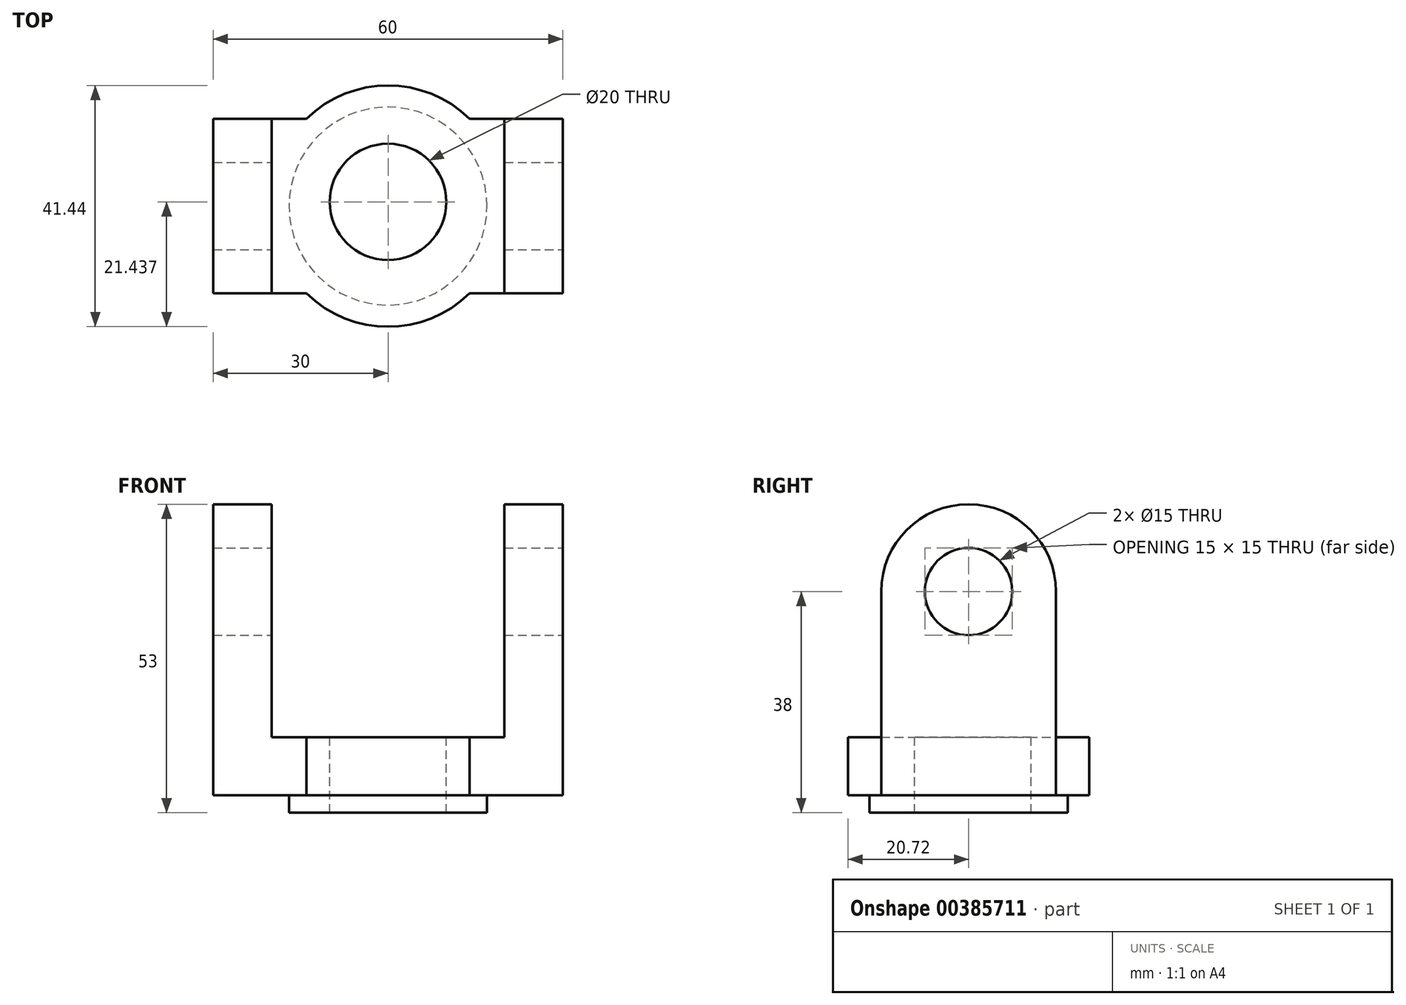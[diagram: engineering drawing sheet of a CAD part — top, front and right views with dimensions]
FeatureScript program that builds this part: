
annotation { "Feature Type Name" : "Feature", "Feature Type Description" : "" }
export const myFeature = defineFeature(function(context is Context, id is Id, definition is map)
    precondition{}
    {
        {
            var Q0;
            Q0=qCreatedBy(makeId("Front.planeOp"),FACE);
            var sketch = newSketch(context, id + "F0", { "sketchPlane" : qUnion([Q0])});
            skLineSegment(sketch, "E0", {"start": v(0, 0) * mm, "end": v(0, 35) * mm});
            skLineSegment(sketch, "E1", {"start": v(0, 35) * mm, "end": v(10, 35) * mm});
            skLineSegment(sketch, "E2", {"start": v(10, 35) * mm, "end": v(10, 10) * mm});
            skLineSegment(sketch, "E3", {"start": v(10, 10) * mm, "end": v(50, 10) * mm});
            skLineSegment(sketch, "E4", {"start": v(50, 10) * mm, "end": v(50, 35) * mm});
            skLineSegment(sketch, "E5", {"start": v(50, 35) * mm, "end": v(60, 35) * mm});
            skLineSegment(sketch, "E6", {"start": v(60, 35) * mm, "end": v(60, 0) * mm});
            skLineSegment(sketch, "E7", {"start": v(0, 0) * mm, "end": v(60, 0) * mm});
            skSolve(sketch);
        }
        {
            var Q0;
            Q0 = qSketchRegion(id + "F0", true);
            extrude(context, id + "F1", {"entities" : qUnion([Q0]), "depth" : 30 * mm});
        }
        {
            var Q0;
            Q0=qCreatedBy(makeId("Right.planeOp"),FACE);
            var sketch = newSketch(context, id + "F2", { "sketchPlane" : qUnion([Q0])});
            skArc(sketch, "E8", {"start": v(0, 35) * mm, "mid": v(-15, 50) * mm, "end": v(-30, 35) * mm});
            skLineSegment(sketch, "E9", {"start": v(-30, 35) * mm, "end": v(0, 35) * mm});
            skSolve(sketch);
        }
        {
            var Q0;
            Q0 = qSketchRegion(id + "F2", true);
            extrude(context, id + "F3", {"entities" : qUnion([Q0]), "operationType" : NewBodyOperationType.ADD, "depth" : 60 * mm});
        }
        {
            var Q0;
            Q0=makeQuery(id+"F3.boolean.opBoolean","MERGE",FACE,{"derivedFrom":[makeQuery(id+"F1.opExtrude","SWEPT_FACE",FACE,{"disambiguationData":[OSD([sQuery(id+"F0.wireOp",EDGE,"E6")])]}),makeQuery(id+"F3.opExtrude","CAP_FACE",FACE,{"disambiguationData":[OSD([sQuery(id+"F2.wireOp",EDGE,"E8"),sQuery(id+"F2.wireOp",EDGE,"E9")])],"isStart":false})]});
            var sketch = newSketch(context, id + "F4", { "sketchPlane" : qUnion([Q0])});
            skCircle(sketch, "E10", {"center": v(-15, 35) * mm, "radius": 7.5 * mm});
            skSolve(sketch);
        }
        {
            var Q0;
            Q0 = qSketchRegion(id + "F4", true);
            extrude(context, id + "F5", {"entities" : qUnion([Q0]), "operationType" : NewBodyOperationType.REMOVE, "endBound" : BoundingType.THROUGH_ALL, "oppositeDirection" : true, "depth" : 25 * mm});
        }
        {
            var Q0;
            Q0=qCreatedBy(makeId("Front.planeOp"),FACE);
            var sketch = newSketch(context, id + "F6", { "sketchPlane" : qUnion([Q0])});
            skLineSegment(sketch, "E11.bottom", {"start": v(10, 10) * mm, "end": v(50, 10) * mm});
            skLineSegment(sketch, "E11.top", {"start": v(10, 50) * mm, "end": v(50, 50) * mm});
            skLineSegment(sketch, "E11.left", {"start": v(10, 10) * mm, "end": v(10, 50) * mm});
            skLineSegment(sketch, "E11.right", {"start": v(50, 10) * mm, "end": v(50, 50) * mm});
            skSolve(sketch);
        }
        {
            var Q0;
            Q0 = qSketchRegion(id + "F6", true);
            extrude(context, id + "F7", {"entities" : qUnion([Q0]), "operationType" : NewBodyOperationType.REMOVE, "endBound" : BoundingType.THROUGH_ALL, "depth" : 25 * mm});
        }
        {
            var Q0;
            Q0=makeQuery(id+"F1.opExtrude","SWEPT_FACE",FACE,{"disambiguationData":[OSD([sQuery(id+"F0.wireOp",EDGE,"E3")])]});
            var sketch = newSketch(context, id + "F8", { "sketchPlane" : qUnion([Q0])});
            skCircle(sketch, "E12", {"center": v(30, -15) * mm, "radius": 17 * mm});
            skPoint(sketch, "E12.centerSnap0", {"position": v(30, 0) * mm});
            skSolve(sketch);
        }
        {
            var Q0;
            Q0 = qSketchRegion(id + "F8", true);
            extrude(context, id + "F9", {"entities" : qUnion([Q0]), "operationType" : NewBodyOperationType.ADD, "oppositeDirection" : true, "depth" : 13 * mm});
        }
        {
            var Q0;
            Q0=makeQuery(id+"F9.boolean.opBoolean","MERGE",FACE,{"derivedFrom":[makeQuery(id+"F1.opExtrude","SWEPT_FACE",FACE,{"disambiguationData":[OSD([sQuery(id+"F0.wireOp",EDGE,"E3")])]}),makeQuery(id+"F9.opExtrude","CAP_FACE",FACE,{"disambiguationData":[OSD([sQuery(id+"F8.wireOp",EDGE,"E12")])],"isStart":true})]});
            var sketch = newSketch(context, id + "F10", { "sketchPlane" : qUnion([Q0])});
            skArc(sketch, "E13", {"start": v(44, 0) * mm, "mid": v(30, 5.72) * mm, "end": v(16, 0) * mm});
            skArc(sketch, "E14", {"start": v(16, -30) * mm, "mid": v(30, -35.72) * mm, "end": v(44, -30) * mm});
            skLineSegment(sketch, "E15", {"start": v(16, 0) * mm, "end": v(44, 0) * mm});
            skLineSegment(sketch, "E16", {"start": v(44, -30) * mm, "end": v(16, -30) * mm});
            skSolve(sketch);
        }
        {
            var Q0;
            Q0 = qSketchRegion(id + "F10", true);
            extrude(context, id + "F11", {"entities" : qUnion([Q0]), "operationType" : NewBodyOperationType.ADD, "oppositeDirection" : true, "depth" : 10 * mm});
        }
        {
            var Q0;
            Q0=makeQuery(id+"F11.boolean.opBoolean","MERGE",FACE,{"derivedFrom":[makeQuery(id+"F9.boolean.opBoolean","MERGE",FACE,{"derivedFrom":[makeQuery(id+"F1.opExtrude","SWEPT_FACE",FACE,{"disambiguationData":[OSD([sQuery(id+"F0.wireOp",EDGE,"E3")])]}),makeQuery(id+"F9.opExtrude","CAP_FACE",FACE,{"disambiguationData":[OSD([sQuery(id+"F8.wireOp",EDGE,"E12")])],"isStart":true})]}),makeQuery(id+"F11.opExtrude","CAP_FACE",FACE,{"disambiguationData":[OSD([sQuery(id+"F10.wireOp",EDGE,"E13"),sQuery(id+"F10.wireOp",EDGE,"E15")])],"isStart":true}),makeQuery(id+"F11.opExtrude","CAP_FACE",FACE,{"disambiguationData":[OSD([sQuery(id+"F10.wireOp",EDGE,"E14"),sQuery(id+"F10.wireOp",EDGE,"E16")])],"isStart":true})]});
            var sketch = newSketch(context, id + "F12", { "sketchPlane" : qUnion([Q0])});
            skCircle(sketch, "E17", {"center": v(30, -14.28) * mm, "radius": 10 * mm});
            skSolve(sketch);
        }
        {
            var Q0;
            Q0 = qSketchRegion(id + "F12", true);
            extrude(context, id + "F13", {"entities" : qUnion([Q0]), "operationType" : NewBodyOperationType.REMOVE, "endBound" : BoundingType.THROUGH_ALL, "oppositeDirection" : true, "depth" : 25 * mm});
        }
    });
